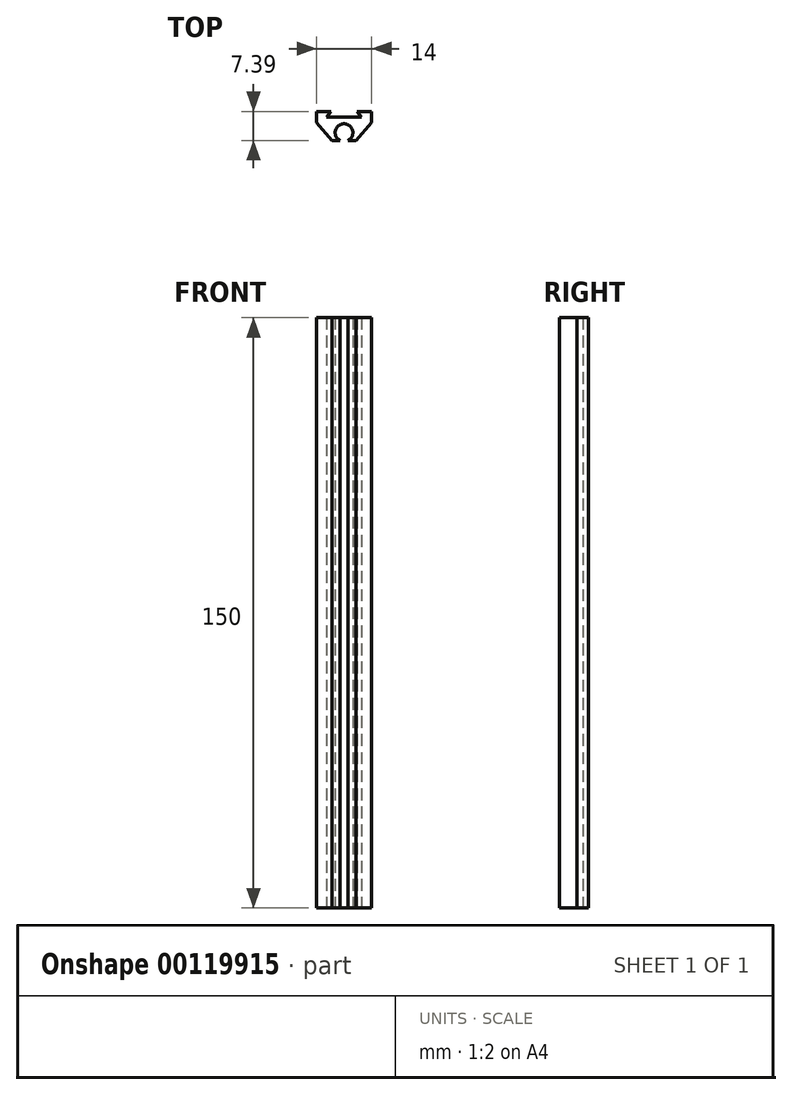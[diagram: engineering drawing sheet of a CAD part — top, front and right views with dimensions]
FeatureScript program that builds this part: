
annotation { "Feature Type Name" : "Feature", "Feature Type Description" : "" }
export const myFeature = defineFeature(function(context is Context, id is Id, definition is map)
    precondition{}
    {
        {
            var Q0;
            Q0=qCreatedBy(makeId("Top.planeOp"),FACE);
            var sketch = newSketch(context, id + "F0", { "sketchPlane" : qUnion([Q0])});
            skLineSegment(sketch, "E0.bottom", {"start": v(7, -3.59) * mm, "end": v(-7, -3.59) * mm});
            skLineSegment(sketch, "E0.top", {"start": v(7, -5.09) * mm, "end": v(-7, -5.09) * mm});
            skLineSegment(sketch, "E0.left", {"start": v(7, -3.59) * mm, "end": v(7, -5.09) * mm});
            skLineSegment(sketch, "E0.right", {"start": v(-7, -3.59) * mm, "end": v(-7, -5.09) * mm});
            skPoint(sketch, "E0.middle", {"position": v(0, -4.34) * mm});
            skLineSegment(sketch, "E1", {"start": v(0, 2.23) * mm, "end": v(0, -20.15) * mm, "construction": true});
            skArc(sketch, "E2", {"start": v(1, -9.6) * mm, "mid": v(0, -5.34) * mm, "end": v(-1, -9.6) * mm});
            skLineSegment(sketch, "E3", {"start": v(-1, -9.6) * mm, "end": v(-3, -9.6) * mm});
            skLineSegment(sketch, "E4", {"start": v(-3, -9.6) * mm, "end": v(-7, -5.09) * mm});
            skLineSegment(sketch, "E5", {"start": v(1, -9.6) * mm, "end": v(3, -9.6) * mm});
            skLineSegment(sketch, "E6", {"start": v(3, -9.6) * mm, "end": v(7, -5.09) * mm});
            skLineSegment(sketch, "E7", {"start": v(-4.5, -3.59) * mm, "end": v(-3.34, -2.2) * mm});
            skLineSegment(sketch, "E8", {"start": v(-3.34, -2.2) * mm, "end": v(-7, -2.2) * mm});
            skLineSegment(sketch, "E9", {"start": v(-7, -2.2) * mm, "end": v(-7, -3.59) * mm});
            skLineSegment(sketch, "E10.MirrorCS", {"start": v(7, -2.2) * mm, "end": v(7, -3.59) * mm});
            skLineSegment(sketch, "E11.MirrorCS", {"start": v(4.5, -3.59) * mm, "end": v(3.34, -2.2) * mm});
            skLineSegment(sketch, "E12.MirrorCS", {"start": v(3.34, -2.2) * mm, "end": v(7, -2.2) * mm});
            skSolve(sketch);
        }
        {
            var Q0;
            Q0 = qSketchRegion(id + "F0", true);
            extrude(context, id + "F1", {"entities" : qUnion([Q0]), "depth" : 150 * mm});
        }
    });
